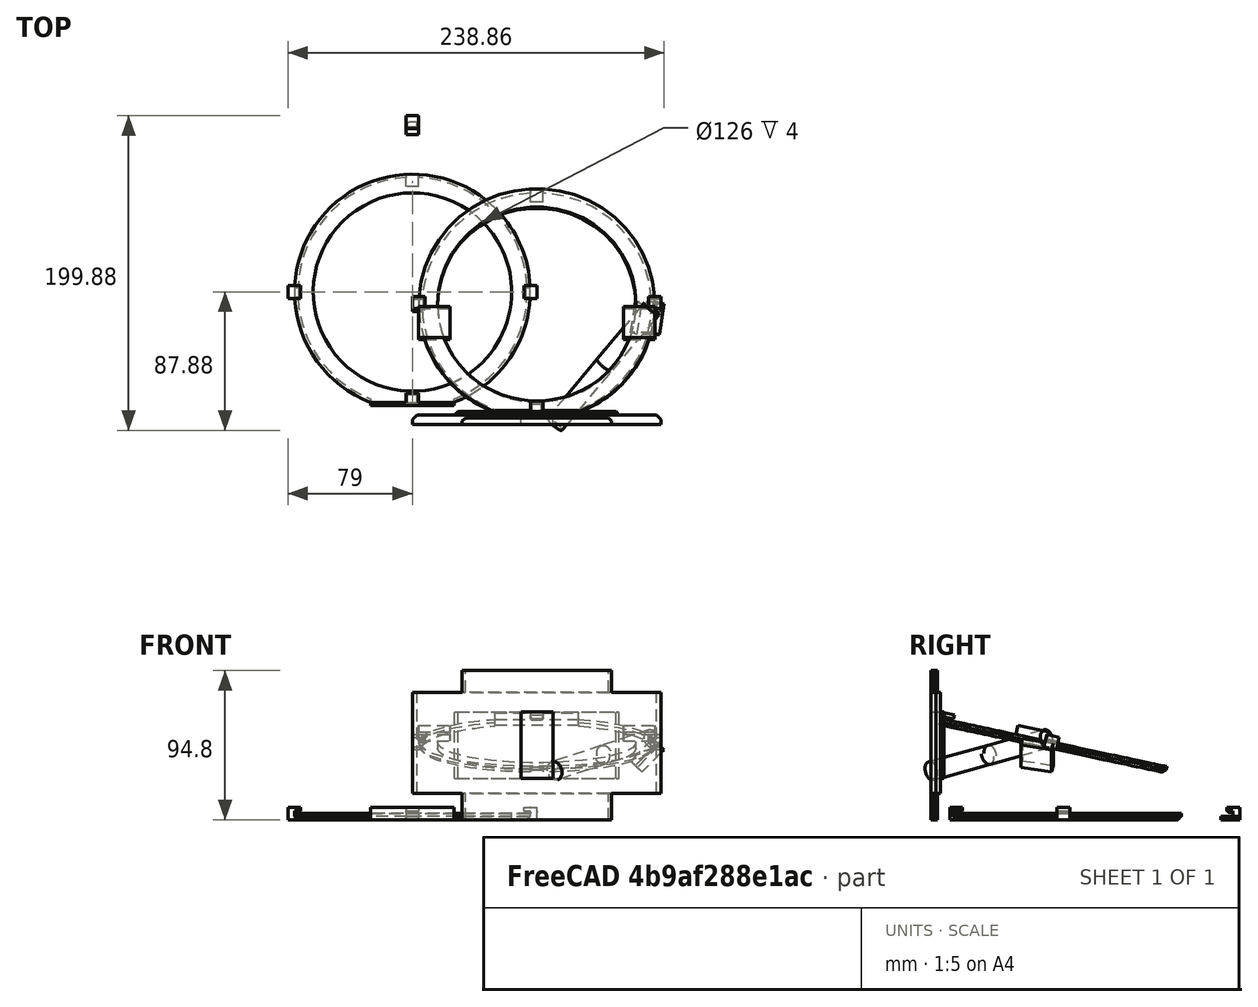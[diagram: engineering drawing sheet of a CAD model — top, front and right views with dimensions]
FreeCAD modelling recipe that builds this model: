
FCSTD DOCUMENT  (FreeCAD 0.19R0.19.2)
Label: waferHolder_020
License: All rights reserved
LicenseURL: http://en.wikipedia.org/wiki/All_rights_reserved
objects: Part::Box×36, Part::Chamfer×28, Part::MultiFuse×12, Part::Cut×10, Part::Cylinder×8, Sketcher::SketchObject×7, Part::Extrusion×7, Part::Fuse×2, Part::Mirroring×2, App::MeasureDistance×1
note: 112 computed .brp shape members not serialized (recipe doc carries the construction recipe); baked Part::Feature solids carry a one-line shape summary decoded from their .brp

FEATURE [Part::Box] Box003  label="bitHolderTop"
  AttacherType = Attacher::AttachEngine3D
  Height = 2
  Length = 8
  Placement = pos=(-4,100,0) rot=(0,0,1;0rad)
  Width = 12
FEATURE [Part::Box] Box008  label="holderBitLeft003"
  AttacherType = Attacher::AttachEngine3D
  Height = 2
  Length = 8
  Placement = pos=(-4,71,2) rot=(0,0,1;0rad)
  Width = 8
FEATURE [Part::Box] Box009  label="bitHolderTopCutout001"
  AttacherType = Attacher::AttachEngine3D
  Height = 4
  Length = 8
  Placement = pos=(-4,67,-2) rot=(0,0,1;0rad)
  Width = 12
FEATURE [Sketcher::SketchObject] Sketch002
  FullyConstrained = true
  sketch-geometry (3):
    g0: Circle CenterX=-3.1415e-12 CenterY=5.6243e-12 CenterZ=0 NormalX=0 NormalY=0 NormalZ=1 AngleXU=0 Radius=63
    g1: ArcOfCircle CenterX=-3.1415e-12 CenterY=5.6243e-12 CenterZ=0 NormalX=0 NormalY=0 NormalZ=1 AngleXU=0 Radius=74.8482 StartAngle=5.07429 EndAngle=10.6337
    g2: LineSegment StartX=-26.5 StartY=-70.0001 StartZ=0 EndX=26.5 EndY=-70.0001 EndZ=0
  constraints (6):
    c: Block(g0)
    c: Coincident(g1,g0)
    c: Block(g1)
    c: Coincident(g2,g1)
    c: Coincident(g2,g1)
    c: Horizontal(g2)
FEATURE [Part::Extrusion] Extrude002  label="mainHolderRing003"
  Base = -> Sketch002
  Dir = (0,0,1)
  DirMode = 2
  FaceMakerClass = Part::FaceMakerBullseye
  LengthFwd = 4
  LengthRev = 0
  Solid = true
  Symmetric = false
FEATURE [Part::Chamfer] Chamfer001
  Base = -> Extrude002
  Edges = 1 edges r=2: [Edge3]
FEATURE [Part::Cut] Cut002  label="mainHolderRing004"
  Base = -> Chamfer001
  Tool = -> Box009
FEATURE [Part::Cut] Cut003  label="bitHolderTop001"
  Base = -> Box008
  Tool = -> Cut002
FEATURE [Part::Box] Box010  label="holderBitLeft004"
  AttacherType = Attacher::AttachEngine3D
  Height = 2
  Length = 8
  Placement = pos=(-4,71,2) rot=(0,0,1;0rad)
  Width = 8
FEATURE [Part::Box] Box011  label="bitHolderTopCutout002"
  AttacherType = Attacher::AttachEngine3D
  Height = 4
  Length = 8
  Placement = pos=(-4,67,-2) rot=(0,0,1;0rad)
  Width = 12
FEATURE [Sketcher::SketchObject] Sketch003
  FullyConstrained = true
  sketch-geometry (3):
    g0: Circle CenterX=-3.1415e-12 CenterY=5.6243e-12 CenterZ=0 NormalX=0 NormalY=0 NormalZ=1 AngleXU=0 Radius=63
    g1: ArcOfCircle CenterX=-3.1415e-12 CenterY=5.6243e-12 CenterZ=0 NormalX=0 NormalY=0 NormalZ=1 AngleXU=0 Radius=74.8482 StartAngle=5.07429 EndAngle=10.6337
    g2: LineSegment StartX=-26.5 StartY=-70.0001 StartZ=0 EndX=26.5 EndY=-70.0001 EndZ=0
  constraints (6):
    c: Block(g0)
    c: Coincident(g1,g0)
    c: Block(g1)
    c: Coincident(g2,g1)
    c: Coincident(g2,g1)
    c: Horizontal(g2)
FEATURE [Part::Extrusion] Extrude003  label="mainHolderRing006"
  Base = -> Sketch003
  Dir = (0,0,1)
  DirMode = 2
  FaceMakerClass = Part::FaceMakerBullseye
  LengthFwd = 4
  LengthRev = 0
  Solid = true
  Symmetric = false
FEATURE [Part::Chamfer] Chamfer002
  Base = -> Extrude003
  Edges = 1 edges r=2: [Edge3]
FEATURE [Part::Cut] Cut005  label="mainHolderRing005"
  Base = -> Chamfer002
  Tool = -> Box011
FEATURE [Part::Cut] Cut004  label="bitHolderTop002"
  Base = -> Box010
  Placement = pos=(0,0,2) rot=(0,0,1;0rad)
  Tool = -> Cut005
FEATURE [Part::Box] Box012  label="holderBitLeft005"
  AttacherType = Attacher::AttachEngine3D
  Height = 2
  Length = 8
  Placement = pos=(-4,71,2) rot=(0,0,1;0rad)
  Width = 8
FEATURE [Part::Box] Box013  label="bitHolderTopCutout003"
  AttacherType = Attacher::AttachEngine3D
  Height = 4
  Length = 8
  Placement = pos=(-4,67,-2) rot=(0,0,1;0rad)
  Width = 12
FEATURE [Sketcher::SketchObject] Sketch004
  FullyConstrained = true
  sketch-geometry (3):
    g0: Circle CenterX=-3.1415e-12 CenterY=5.6243e-12 CenterZ=0 NormalX=0 NormalY=0 NormalZ=1 AngleXU=0 Radius=63
    g1: ArcOfCircle CenterX=-3.1415e-12 CenterY=5.6243e-12 CenterZ=0 NormalX=0 NormalY=0 NormalZ=1 AngleXU=0 Radius=74.8482 StartAngle=5.07429 EndAngle=10.6337
    g2: LineSegment StartX=-26.5 StartY=-70.0001 StartZ=0 EndX=26.5 EndY=-70.0001 EndZ=0
  constraints (6):
    c: Block(g0)
    c: Coincident(g1,g0)
    c: Block(g1)
    c: Coincident(g2,g1)
    c: Coincident(g2,g1)
    c: Horizontal(g2)
FEATURE [Part::Extrusion] Extrude004  label="mainHolderRing008"
  Base = -> Sketch004
  Dir = (0,0,1)
  DirMode = 2
  FaceMakerClass = Part::FaceMakerBullseye
  LengthFwd = 4
  LengthRev = 0
  Solid = true
  Symmetric = false
FEATURE [Part::Chamfer] Chamfer003
  Base = -> Extrude004
  Edges = 1 edges r=2: [Edge3]
FEATURE [Part::Cut] Cut007  label="mainHolderRing007"
  Base = -> Chamfer003
  Tool = -> Box013
FEATURE [Part::Cut] Cut006  label="bitHolderTop003"
  Base = -> Box012
  Placement = pos=(0,0,4) rot=(0,0,1;0rad)
  Tool = -> Cut007
FEATURE [Part::Box] Box014  label="bitHoldertop006"
  AttacherType = Attacher::AttachEngine3D
  Height = 3.4
  Length = 8
  Placement = pos=(-4,71,4.6) rot=(0,0,1;0rad)
  Width = 8
FEATURE [Part::MultiFuse] Fusion001  label="holderTop"
  Placement = pos=(0,33,0) rot=(0,0,1;0rad)
  Shapes = -> [Cut003,Cut004,Cut006,Box014]
FEATURE [Part::Chamfer] Chamfer004
  Base = -> Fusion001
  Edges = 1 edges r=1: [Edge16]
FEATURE [Part::Chamfer] Chamfer009
  Base = -> Chamfer004
  Edges = 1 edges r=1: [Edge1]
FEATURE [Part::Chamfer] Chamfer010
  Base = -> Chamfer009
  Edges = 1 edges r=1: [Edge32]
FEATURE [Part::Box] Box018  label="base001"
  AttacherType = Attacher::AttachEngine3D
  Height = 64.44
  Length = 158
  Placement = pos=(0,-84,16.6) rot=(0,0,1;0rad)
  Width = 6
FEATURE [Part::Box] Box019  label="base002"
  AttacherType = Attacher::AttachEngine3D
  Height = 94.8
  Length = 94.8
  Placement = pos=(31.6,-84,0) rot=(0,0,1;0rad)
  Width = 4
FEATURE [Part::Box] Box020  label="base003"
  AttacherType = Attacher::AttachEngine3D
  Height = 42.44
  Length = 104.28
  Placement = pos=(26.86,-84,26.18) rot=(0,0,1;0rad)
  Width = 8
FEATURE [Part::Chamfer] Chamfer014
  Base = -> Box018
  Edges = 1 edges r=3: [Edge3]
FEATURE [Part::Chamfer] Chamfer015
  Base = -> Chamfer014
  Edges = 1 edges r=3: [Edge15]
FEATURE [Part::Chamfer] Chamfer016
  Base = -> Box019
  Edges = 1 edges r=2: [Edge3]
FEATURE [Part::Chamfer] Chamfer017
  Base = -> Box020
  Edges = 1 edges r=2: [Edge3]
FEATURE [Part::Chamfer] Chamfer018
  Base = -> Chamfer016
  Edges = 1 edges r=2: [Edge15]
FEATURE [Part::Chamfer] Chamfer019
  Base = -> Chamfer017
  Edges = 1 edges r=2: [Edge15]
FEATURE [Part::MultiFuse] Fusion002  label="base004"
  Shapes = -> [Chamfer015,Chamfer018,Chamfer019]
FEATURE [Part::Box] Box021  label="holderBitLeft006"
  AttacherType = Attacher::AttachEngine3D
  Height = 4
  Length = 6
  Placement = pos=(-79,-4,0) rot=(0,0,1;0rad)
  Width = 8
FEATURE [Part::Box] Box022  label="holderBitright003"
  AttacherType = Attacher::AttachEngine3D
  Height = 4
  Length = 6
  Placement = pos=(73,-4,0) rot=(0,0,1;0rad)
  Width = 8
FEATURE [Part::Box] Box023  label="holderBitLeft007"
  AttacherType = Attacher::AttachEngine3D
  Height = 3.4
  Length = 8
  Placement = pos=(-79,-4,4.6) rot=(0,0,1;0rad)
  Width = 8
FEATURE [Part::Box] Box024  label="holderBitRight003"
  AttacherType = Attacher::AttachEngine3D
  Height = 3.4
  Length = 8
  Placement = pos=(71,-4,4.6) rot=(0,0,1;0rad)
  Width = 8
FEATURE [Sketcher::SketchObject] Sketch005
  FullyConstrained = true
  sketch-geometry (3):
    g0: Circle CenterX=-3.1415e-12 CenterY=5.6243e-12 CenterZ=0 NormalX=0 NormalY=0 NormalZ=1 AngleXU=0 Radius=63
    g1: ArcOfCircle CenterX=-3.1415e-12 CenterY=5.6243e-12 CenterZ=0 NormalX=0 NormalY=0 NormalZ=1 AngleXU=0 Radius=74.8482 StartAngle=5.07429 EndAngle=10.6337
    g2: LineSegment StartX=-26.5 StartY=-70.0001 StartZ=0 EndX=26.5 EndY=-70.0001 EndZ=0
  constraints (6):
    c: Block(g0)
    c: Coincident(g1,g0)
    c: Block(g1)
    c: Coincident(g2,g1)
    c: Coincident(g2,g1)
    c: Horizontal(g2)
FEATURE [Part::Box] Box025  label="holderBitLeft008"
  AttacherType = Attacher::AttachEngine3D
  Height = 4
  Length = 8
  Placement = pos=(-79,-4,0) rot=(0,0,1;0rad)
  Width = 8
FEATURE [Part::Box] Box026  label="bitHolderTopCutout004"
  AttacherType = Attacher::AttachEngine3D
  Height = 4
  Length = 8
  Placement = pos=(-4,67,-2) rot=(0,0,1;0rad)
  Width = 12
FEATURE [Part::Extrusion] Extrude006  label="mainHolderRing010"
  Base = -> Sketch005
  Dir = (0,0,1)
  DirMode = 2
  FaceMakerClass = Part::FaceMakerBullseye
  LengthFwd = 4
  LengthRev = 0
  Solid = true
  Symmetric = false
FEATURE [Part::Box] Box027  label="holderBitRight004"
  AttacherType = Attacher::AttachEngine3D
  Height = 4
  Length = 8
  Placement = pos=(71,-4,0) rot=(0,0,1;0rad)
  Width = 8
FEATURE [Part::Chamfer] Chamfer020
  Base = -> Extrude006
  Edges = 1 edges r=2: [Edge3]
FEATURE [Part::Cut] Cut008  label="mainHolderRing011"
  Base = -> Chamfer020
  Tool = -> Box026
FEATURE [Part::MultiFuse] Fusion004  label="holders001"
  Shapes = -> [Box021,Box022]
FEATURE [Sketcher::SketchObject] Sketch006
  FullyConstrained = true
  sketch-geometry (3):
    g0: Circle CenterX=-3.1415e-12 CenterY=5.6243e-12 CenterZ=0 NormalX=0 NormalY=0 NormalZ=1 AngleXU=0 Radius=63
    g1: ArcOfCircle CenterX=-3.1415e-12 CenterY=5.6243e-12 CenterZ=0 NormalX=0 NormalY=0 NormalZ=1 AngleXU=0 Radius=74.8482 StartAngle=5.07429 EndAngle=10.6337
    g2: LineSegment StartX=-26.5 StartY=-70.0001 StartZ=0 EndX=26.5 EndY=-70.0001 EndZ=0
  constraints (6):
    c: Block(g0)
    c: Coincident(g1,g0)
    c: Block(g1)
    c: Coincident(g2,g1)
    c: Coincident(g2,g1)
    c: Horizontal(g2)
FEATURE [Part::Extrusion] Extrude005  label="mainHolderRing009"
  Base = -> Sketch006
  Dir = (0,0,1)
  DirMode = 2
  FaceMakerClass = Part::FaceMakerBullseye
  LengthFwd = 4
  LengthRev = 0
  Solid = true
  Symmetric = false
FEATURE [Part::Cut] Cut009  label="leftAndRightHolderBits001"
  Base = -> Fusion004
  Placement = pos=(0,0,4) rot=(0,0,1;0rad)
  Tool = -> Extrude005
FEATURE [Part::Chamfer] Chamfer021
  Base = -> Box023
  Edges = 1 edges r=1: [Edge8]
FEATURE [Part::Chamfer] Chamfer022
  Base = -> Box024
  Edges = 1 edges r=1: [Edge4]
FEATURE [Part::Chamfer] Chamfer023
  Base = -> Chamfer022
  Edges = 1 edges r=1: [Edge13]
FEATURE [Part::Chamfer] Chamfer024
  Base = -> Chamfer023
  Edges = 1 edges r=1: [Edge5]
FEATURE [Part::Box] Box028  label="holderBottom004"
  AttacherType = Attacher::AttachEngine3D
  Height = 4
  Length = 53
  Placement = pos=(-26.5,-72,0) rot=(0,0,1;0rad)
  Width = 4.5
FEATURE [Part::Chamfer] Chamfer025
  Base = -> Chamfer021
  Edges = 1 edges r=1: [Edge5]
FEATURE [Part::Chamfer] Chamfer026
  Base = -> Chamfer025
  Edges = 1 edges r=1: [Edge16]
FEATURE [Part::Box] Box029  label="holderBottom006"
  AttacherType = Attacher::AttachEngine3D
  Height = 4
  Length = 53
  Placement = pos=(-26.5,-72,4) rot=(0,0,1;0rad)
  Width = 2
FEATURE [Part::Box] Box030  label="holderBottom007"
  AttacherType = Attacher::AttachEngine3D
  Height = 3.4
  Length = 8
  Placement = pos=(-4,-72,4.6) rot=(0,0,1;0rad)
  Width = 8
FEATURE [Part::Chamfer] Chamfer027  label="holderBottom005"
  Base = -> Box030
  Edges = 3 edges r=1: [Edge4,Edge8,Edge11]
FEATURE [Part::MultiFuse] Fusion005  label="removeRingHolder"
  Placement = pos=(79,-8.35,45.4) rot=(1,0,0;6.07375rad)
  Shapes = -> [Box025,Box027,Cut008,Cut009,Chamfer024,Chamfer026,Box028,Box029,Chamfer027]
FEATURE [Part::Box] Box017  label="holderBottom002"
  AttacherType = Attacher::AttachEngine3D
  Height = 3.4
  Length = 8
  Placement = pos=(-4,-72,4.6) rot=(0,0,1;0rad)
  Width = 8
FEATURE [Part::Chamfer] Chamfer013  label="holderBottom003"
  Base = -> Box017
  Edges = 3 edges r=1: [Edge4,Edge8,Edge11]
FEATURE [Part::Box] Box016  label="holderBottom001"
  AttacherType = Attacher::AttachEngine3D
  Height = 4
  Length = 53
  Placement = pos=(-26.5,-72,4) rot=(0,0,1;0rad)
  Width = 2
FEATURE [Part::Box] Box015  label="holderBottom"
  AttacherType = Attacher::AttachEngine3D
  Height = 4
  Length = 53
  Placement = pos=(-26.5,-72,0) rot=(0,0,1;0rad)
  Width = 4.5
FEATURE [Part::Box] Box006  label="holderBitLeft002"
  AttacherType = Attacher::AttachEngine3D
  Height = 3.4
  Length = 8
  Placement = pos=(-79,-4,4.6) rot=(0,0,1;0rad)
  Width = 8
FEATURE [Part::Chamfer] Chamfer005
  Base = -> Box006
  Edges = 1 edges r=1: [Edge8]
FEATURE [Part::Chamfer] Chamfer011
  Base = -> Chamfer005
  Edges = 1 edges r=1: [Edge5]
FEATURE [Part::Chamfer] Chamfer012
  Base = -> Chamfer011
  Edges = 1 edges r=1: [Edge16]
FEATURE [Part::Box] Box007  label="holderBitRight002"
  AttacherType = Attacher::AttachEngine3D
  Height = 3.4
  Length = 8
  Placement = pos=(71,-4,4.6) rot=(0,0,1;0rad)
  Width = 8
FEATURE [Part::Chamfer] Chamfer006
  Base = -> Box007
  Edges = 1 edges r=1: [Edge4]
FEATURE [Part::Chamfer] Chamfer007
  Base = -> Chamfer006
  Edges = 1 edges r=1: [Edge13]
FEATURE [Part::Chamfer] Chamfer008
  Base = -> Chamfer007
  Edges = 1 edges r=1: [Edge5]
FEATURE [Sketcher::SketchObject] Sketch001
  FullyConstrained = true
  sketch-geometry (3):
    g0: Circle CenterX=-3.1415e-12 CenterY=5.6243e-12 CenterZ=0 NormalX=0 NormalY=0 NormalZ=1 AngleXU=0 Radius=63
    g1: ArcOfCircle CenterX=-3.1415e-12 CenterY=5.6243e-12 CenterZ=0 NormalX=0 NormalY=0 NormalZ=1 AngleXU=0 Radius=74.8482 StartAngle=5.07429 EndAngle=10.6337
    g2: LineSegment StartX=-26.5 StartY=-70.0001 StartZ=0 EndX=26.5 EndY=-70.0001 EndZ=0
  constraints (6):
    c: Block(g0)
    c: Coincident(g1,g0)
    c: Block(g1)
    c: Coincident(g2,g1)
    c: Coincident(g2,g1)
    c: Horizontal(g2)
FEATURE [Part::Extrusion] Extrude001  label="mainHolderRing002"
  Base = -> Sketch001
  Dir = (0,0,1)
  DirMode = 2
  FaceMakerClass = Part::FaceMakerBullseye
  LengthFwd = 4
  LengthRev = 0
  Solid = true
  Symmetric = false
FEATURE [Part::Box] Box005  label="holderBitright002"
  AttacherType = Attacher::AttachEngine3D
  Height = 4
  Length = 6
  Placement = pos=(73,-4,0) rot=(0,0,1;0rad)
  Width = 8
FEATURE [Part::Box] Box004  label="holderBitLeft001"
  AttacherType = Attacher::AttachEngine3D
  Height = 4
  Length = 6
  Placement = pos=(-79,-4,0) rot=(0,0,1;0rad)
  Width = 8
FEATURE [Part::MultiFuse] Fusion  label="holders"
  Shapes = -> [Box004,Box005]
FEATURE [Part::Cut] Cut001  label="leftAndRightHolderBits"
  Base = -> Fusion
  Placement = pos=(0,0,4) rot=(0,0,1;0rad)
  Tool = -> Extrude001
FEATURE [Part::Box] Box001  label="bitHolderTopCutout"
  AttacherType = Attacher::AttachEngine3D
  Height = 4
  Length = 8
  Placement = pos=(-4,67,-2) rot=(0,0,1;0rad)
  Width = 12
FEATURE [Sketcher::SketchObject] Sketch
  FullyConstrained = true
  sketch-geometry (3):
    g0: Circle CenterX=-3.1415e-12 CenterY=5.6243e-12 CenterZ=0 NormalX=0 NormalY=0 NormalZ=1 AngleXU=0 Radius=63
    g1: ArcOfCircle CenterX=-3.1415e-12 CenterY=5.6243e-12 CenterZ=0 NormalX=0 NormalY=0 NormalZ=1 AngleXU=0 Radius=74.8482 StartAngle=5.07429 EndAngle=10.6337
    g2: LineSegment StartX=-26.5 StartY=-70.0001 StartZ=0 EndX=26.5 EndY=-70.0001 EndZ=0
  constraints (6):
    c: Block(g0)
    c: Coincident(g1,g0)
    c: Block(g1)
    c: Coincident(g2,g1)
    c: Coincident(g2,g1)
    c: Horizontal(g2)
FEATURE [Part::Extrusion] Extrude  label="mainHolderRing"
  Base = -> Sketch
  Dir = (0,0,1)
  DirMode = 2
  FaceMakerClass = Part::FaceMakerBullseye
  LengthFwd = 4
  LengthRev = 0
  Solid = true
  Symmetric = false
FEATURE [Part::Chamfer] Chamfer
  Base = -> Extrude
  Edges = 1 edges r=2: [Edge3]
FEATURE [Part::Cut] Cut  label="mainHolderRing001"
  Base = -> Chamfer
  Tool = -> Box001
FEATURE [Part::Box] Box002  label="holderBitRight"
  AttacherType = Attacher::AttachEngine3D
  Height = 4
  Length = 8
  Placement = pos=(71,-4,0) rot=(0,0,1;0rad)
  Width = 8
FEATURE [Part::Box] Box  label="holderBitLeft"
  AttacherType = Attacher::AttachEngine3D
  Height = 4
  Length = 8
  Placement = pos=(-79,-4,0) rot=(0,0,1;0rad)
  Width = 8
FEATURE [Part::MultiFuse] Fusion003  label="ringHolder"
  Shapes = -> [Box,Box002,Cut,Cut001,Chamfer008,Chamfer012,Box015,Box016,Chamfer013]
FEATURE [Part::Cylinder] Cylinder
  Angle = 360
  AttacherType = Attacher::AttachEngine3D
  Height = 50
  Placement = pos=(34.86,-30,47.4) rot=(1,0,0;1.5708rad)
  Radius = 6
FEATURE [Part::Box] Box031  label="base005"
  AttacherType = Attacher::AttachEngine3D
  Height = 42.44
  Length = 20.28
  Placement = pos=(68.86,-84,26.18) rot=(0,0,1;0rad)
  Width = 8
FEATURE [Part::Cylinder] Cylinder001
  Angle = 360
  AttacherType = Attacher::AttachEngine3D
  Height = 50
  Placement = pos=(34.86,-30,47.4) rot=(1,0,0;1.5708rad)
  Radius = 6
FEATURE [Part::MultiFuse] Fusion006
  Placement = pos=(0,0,0) rot=(1,0,0;0.20944rad)
  Shapes = -> [Cylinder001,Cylinder]
FEATURE [Part::Cylinder] Cylinder002
  Angle = 360
  AttacherType = Attacher::AttachEngine3D
  Height = 50
  Placement = pos=(34.86,-30,47.4) rot=(1,0,0;1.5708rad)
  Radius = 6
FEATURE [Part::Cylinder] Cylinder003
  Angle = 360
  AttacherType = Attacher::AttachEngine3D
  Height = 50
  Placement = pos=(34.86,-30,47.4) rot=(1,0,0;1.5708rad)
  Radius = 6
FEATURE [Part::MultiFuse] Fusion007
  Placement = pos=(0,0,0) rot=(1,0,0;0.20944rad)
  Shapes = -> [Cylinder003,Cylinder002]
FEATURE [Part::MultiFuse] Fusion008
  Placement = pos=(-44.06,-5,11.27) rot=(0,0,1;0.698132rad)
  Shapes = -> [Fusion007,Fusion006]
FEATURE [App::MeasureDistance] Distance  label="Distance: 0.65 mm"
  Distance = 0.654413
  P1 = (68.86,-76,67.959)
  P2 = (68.8586,-76,68.6134)
FEATURE [Part::Cylinder] Cylinder004
  Angle = 360
  AttacherType = Attacher::AttachEngine3D
  Height = 50
  Placement = pos=(34.86,-30,47.4) rot=(1,0,0;1.5708rad)
  Radius = 6
FEATURE [Part::Cylinder] Cylinder005
  Angle = 360
  AttacherType = Attacher::AttachEngine3D
  Height = 50
  Placement = pos=(34.86,-30,47.4) rot=(1,0,0;1.5708rad)
  Radius = 6
FEATURE [Part::MultiFuse] Fusion010
  Placement = pos=(0,0,0) rot=(1,0,0;0.20944rad)
  Shapes = -> [Cylinder005,Cylinder004]
FEATURE [Part::Cylinder] Cylinder006
  Angle = 360
  AttacherType = Attacher::AttachEngine3D
  Height = 50
  Placement = pos=(34.86,-30,47.4) rot=(1,0,0;1.5708rad)
  Radius = 6
FEATURE [Part::Cylinder] Cylinder007
  Angle = 360
  AttacherType = Attacher::AttachEngine3D
  Height = 50
  Placement = pos=(34.86,-30,47.4) rot=(1,0,0;1.5708rad)
  Radius = 6
FEATURE [Part::MultiFuse] Fusion009
  Placement = pos=(0,0,0) rot=(1,0,0;0.20944rad)
  Shapes = -> [Cylinder007,Cylinder006]
FEATURE [Part::MultiFuse] Fusion011
  Placement = pos=(-14,-40.82,1.35) rot=(0,0,1;0.698132rad)
  Shapes = -> [Fusion009,Fusion010]
FEATURE [Part::Fuse] Fusion012
  Base = -> Fusion008
  Placement = pos=(-1.7,2,0) rot=(0,0,1;0rad)
  Tool = -> Fusion011
FEATURE [Part::Mirroring] Part__Mirroring  label="Fusion012 (Mirror #1)"
  Base = (0,0,0)
  Normal = (1,0,0)
  Placement = pos=(158,0,0) rot=(0,0,1;0rad)
  Source = -> Fusion012
FEATURE [Part::Box] Box032  label="removeStrutLeft"
  AttacherType = Attacher::AttachEngine3D
  Height = 6
  Length = 20
  Placement = pos=(4,-30.1,54.1) rot=(1,0,0;6.07375rad)
  Width = 20
FEATURE [Part::Box] Box033  label="reoveStrustRight"
  AttacherType = Attacher::AttachEngine3D
  Height = 6
  Length = 20
  Placement = pos=(134,-30.1,54.1) rot=(-1,0,0;0.20944rad)
  Width = 20
FEATURE [Part::Box] Box034  label="removeStrutLeft001"
  AttacherType = Attacher::AttachEngine3D
  Height = 6
  Length = 20
  Placement = pos=(4,-30.1,54.1) rot=(-1,0,0;0.20944rad)
  Width = 20
FEATURE [Part::Box] Box035  label="removeStrutLeft002"
  AttacherType = Attacher::AttachEngine3D
  Height = 6
  Length = 20
  Placement = pos=(4,-30.1,54.1) rot=(-1,0,0;0.20944rad)
  Width = 20
FEATURE [Part::Fuse] Fusion013
  Base = -> Box034
  Placement = pos=(-40,3,12) rot=(0,1,0;0.785398rad)
  Tool = -> Box035
FEATURE [Part::Mirroring] Part__Mirroring001  label="Fusion013 (Mirror #2)"
  Base = (0,0,0)
  Normal = (1,0,0)
  Placement = pos=(158,0,0) rot=(0,0,1;0rad)
  Source = -> Fusion013
